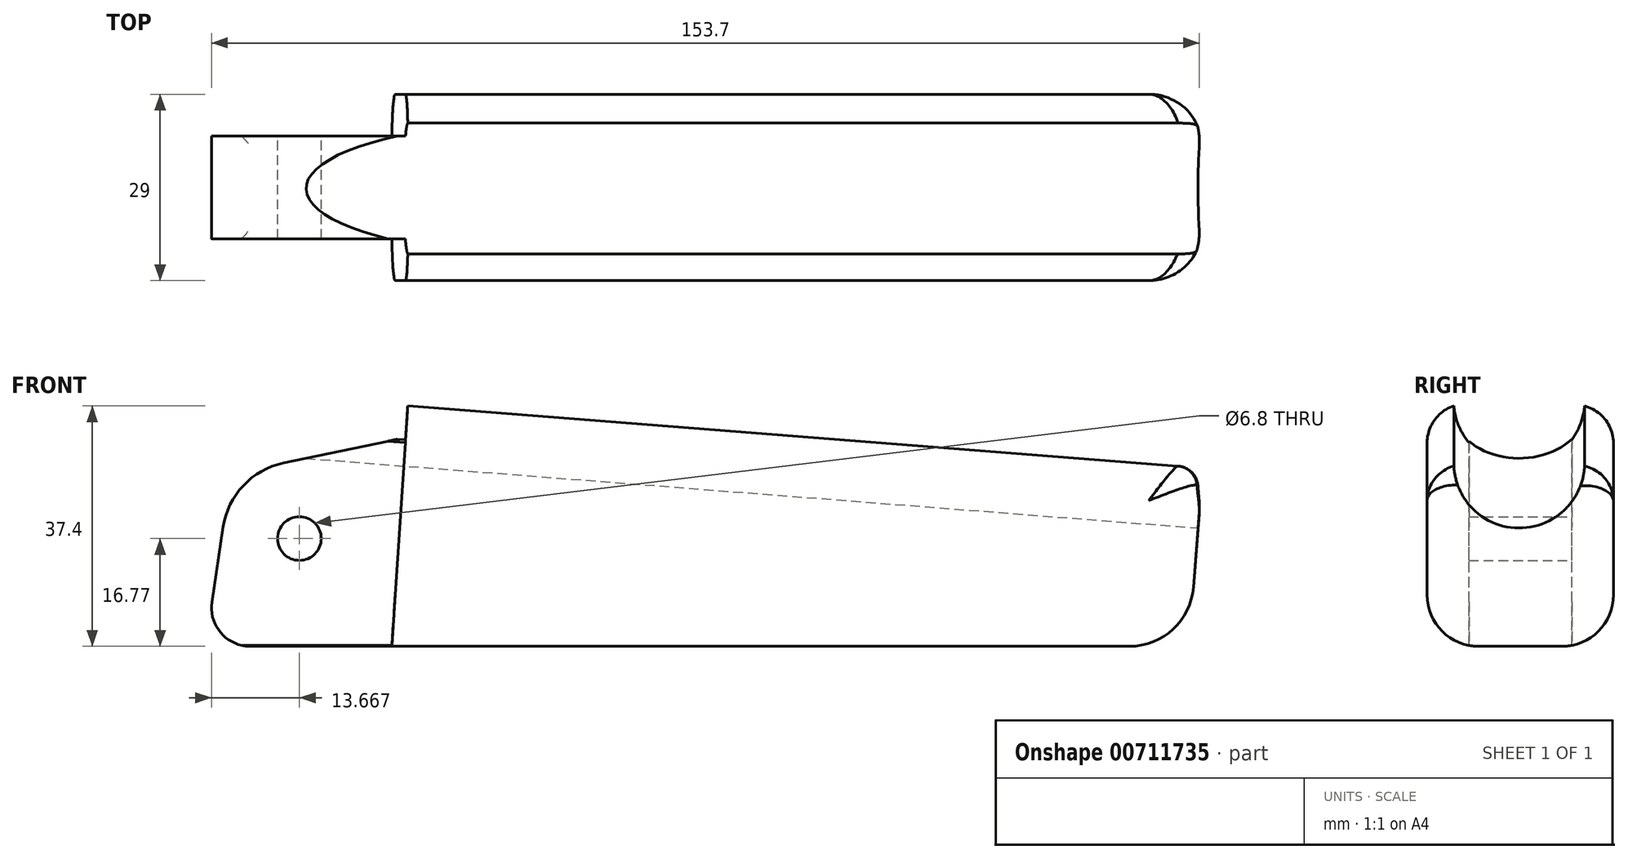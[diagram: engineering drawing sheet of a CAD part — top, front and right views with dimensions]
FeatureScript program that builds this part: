
annotation { "Feature Type Name" : "Feature", "Feature Type Description" : "" }
export const myFeature = defineFeature(function(context is Context, id is Id, definition is map)
    precondition{}
    {
        {
            var Q0;
            Q0=qCreatedBy(makeId("Front.planeOp"),FACE);
            var sketch = newSketch(context, id + "F0", { "sketchPlane" : qUnion([Q0])});
            skLineSegment(sketch, "E0", {"start": v(-23.94, 0) * mm, "end": v(100.06, 0) * mm});
            skLineSegment(sketch, "E1", {"start": v(-21.46, 37.4) * mm, "end": v(102.22, 27.74) * mm});
            skLineSegment(sketch, "E2", {"start": v(102.22, 27.74) * mm, "end": v(100.06, 0) * mm});
            skLineSegment(sketch, "E3", {"start": v(-23.94, 0) * mm, "end": v(-45.99, 0) * mm});
            skCircle(sketch, "E4", {"center": v(-38.32, 16.77) * mm, "radius": 3.4 * mm});
            skArc(sketch, "E5", {"start": v(-40.79, 28.51) * mm, "mid": v(-47.06, 25) * mm, "end": v(-50.2, 18.53) * mm});
            skLineSegment(sketch, "E6", {"start": v(-21.79, 32.5) * mm, "end": v(-40.79, 28.51) * mm});
            skLineSegment(sketch, "E7", {"start": v(-23.94, 0) * mm, "end": v(-21.46, 37.4) * mm});
            skLineSegment(sketch, "E8", {"start": v(-51.92, 6.88) * mm, "end": v(-50.2, 18.53) * mm});
            skArc(sketch, "E9.filletArc", {"start": v(-51.92, 6.88) * mm, "mid": v(-50.53, 2.08) * mm, "end": v(-45.99, 0) * mm});
            skSolve(sketch);
        }
        {
            var Q0;
            Q0=makeQuery(id+"F0.imprint","IMPRINT",FACE,{"disambiguationData":[TD([[makeQuery(id+"F0.imprint","IMPRINT",EDGE,{"derivedFrom":sQuery(id+"F0.wireOp",EDGE,"E0")}),1.0]])]});
            extrude(context, id + "F1", {"entities" : qUnion([Q0]), "endBound" : BoundingType.SYMMETRIC, "depth" : 29 * mm, "offsetDistance" : 25 * mm});
        }
        {
            var Q0;
            Q0 = qSketchRegion(id + "F0", true);
            extrude(context, id + "F2", {"entities" : qUnion([Q0]), "operationType" : NewBodyOperationType.ADD, "endBound" : BoundingType.SYMMETRIC, "depth" : 16 * mm, "offsetDistance" : 25 * mm});
        }
        {
            var Q0;
            Q0=makeQuery(id+"F1.opExtrude","SWEPT_FACE",FACE,{"disambiguationData":[OSD([sQuery(id+"F0.wireOp",EDGE,"E2")])]});
            var sketch = newSketch(context, id + "F3", { "sketchPlane" : qUnion([Q0])});
            skLineSegment(sketch, "E10", {"start": v(-27.87, 26.47) * mm, "end": v(29.15, 26.47) * mm, "construction": true});
            skLineSegment(sketch, "E11", {"start": v(10, 48.39) * mm, "end": v(10, -4.27) * mm, "construction": true});
            skLineSegment(sketch, "E12", {"start": v(-10, 48.02) * mm, "end": v(-10, 0) * mm, "construction": true});
            skCircle(sketch, "E13", {"center": v(-0.17, 36.45) * mm, "radius": 10.2 * mm});
            skPoint(sketch, "E13.first.point", {"position": v(-10, 33.7) * mm});
            skPoint(sketch, "E13.second.point", {"position": v(10, 35.62) * mm});
            skPoint(sketch, "E13.third.point", {"position": v(1.93, 26.47) * mm});
            skSolve(sketch);
        }
        {
            var Q0;
            {var subQ0=sQuery(id+"F3.wireOp",EDGE,"E13");var subQ1=makeQuery(id+"F1.opExtrude","SWEPT_EDGE",EDGE,{"disambiguationData":[OSD([sQuery(id+"F0.wireOp",EDGE,"E1"),sQuery(id+"F0.wireOp",EDGE,"E2")])]});var subQ2=makeQuery(id+"F3.imprint","INTERSECT",VERTEX,{"disambiguationData":[OD(0.0)],"derivedFrom":[subQ1,subQ0]});Q0=makeQuery(id+"F3.imprint","IMPRINT",FACE,{"disambiguationData":[TD([[makeQuery(id+"F3.imprint","IMPRINT",EDGE,{"disambiguationData":[TD([[subQ2,1.0]])],"derivedFrom":subQ0}),1.0]])]});}
            extrude(context, id + "F4", {"entities" : qUnion([Q0]), "operationType" : NewBodyOperationType.REMOVE, "endBound" : BoundingType.THROUGH_ALL, "oppositeDirection" : true, "depth" : 25 * mm, "offsetDistance" : 25 * mm});
        }
        {
            var Q0;
            Q0=makeQuery(id+"F1.opExtrude","CAP_EDGE",EDGE,{"disambiguationData":[OSD([sQuery(id+"F0.wireOp",EDGE,"E1")])],"isStart":false});
            var Q1;
            Q1=makeQuery(id+"F1.opExtrude","CAP_EDGE",EDGE,{"disambiguationData":[OSD([sQuery(id+"F0.wireOp",EDGE,"E1")])],"isStart":true});
            fillet(context, id + "F5", {"entities" : qUnion([Q0, Q1]), "radius" : 6 * mm, "tangentPropagation" : true, "allowEdgeOverflow" : false});
        }
        {
            var Q0;
            Q0=makeQuery(id+"F1.opExtrude","CAP_EDGE",EDGE,{"disambiguationData":[OSD([sQuery(id+"F0.wireOp",EDGE,"E0")])],"isStart":true});
            var Q1;
            Q1=makeQuery(id+"F1.opExtrude","CAP_EDGE",EDGE,{"disambiguationData":[OSD([sQuery(id+"F0.wireOp",EDGE,"E0")])],"isStart":false});
            var Q2;
            Q2=makeQuery(id+"F1.opExtrude","CAP_EDGE",EDGE,{"disambiguationData":[OSD([sQuery(id+"F0.wireOp",EDGE,"E2")])],"isStart":false});
            var Q3;
            Q3=makeQuery(id+"F1.opExtrude","CAP_EDGE",EDGE,{"disambiguationData":[OSD([sQuery(id+"F0.wireOp",EDGE,"E2")])],"isStart":true});
            fillet(context, id + "F6", {"entities" : qUnion([Q0, Q1, Q2, Q3]), "radius" : 8 * mm, "tangentPropagation" : true, "allowEdgeOverflow" : false});
        }
        {
            var Q0;
            {var subQ0=sQuery(id+"F0.wireOp",EDGE,"E1");Q0=makeQuery(id+"F6.opFillet","BLEND_EDGE",EDGE,{"blendedFrom":[makeQuery(id+"F1.opExtrude","CAP_EDGE",EDGE,{"disambiguationData":[OSD([sQuery(id+"F0.wireOp",EDGE,"E2")])],"isStart":false}),makeQuery(id+"F5.opFillet","BLEND_FACE",FACE,{"disambiguationData":[OSD([subQ0]),TDD([makeQuery(id+"F1.opExtrude","CAP_EDGE",EDGE,{"disambiguationData":[OSD([subQ0])],"isStart":false})])]})],"blendedInto":[makeQuery(id+"F5.opFillet","BLEND_FACE",FACE,{"disambiguationData":[OSD([subQ0]),TDD([makeQuery(id+"F1.opExtrude","CAP_EDGE",EDGE,{"disambiguationData":[OSD([subQ0])],"isStart":false})])]})]});}
            var Q1;
            {var subQ0=sQuery(id+"F0.wireOp",EDGE,"E1");Q1=makeQuery(id+"F6.opFillet","BLEND_EDGE",EDGE,{"blendedFrom":[makeQuery(id+"F1.opExtrude","CAP_EDGE",EDGE,{"disambiguationData":[OSD([sQuery(id+"F0.wireOp",EDGE,"E2")])],"isStart":true}),makeQuery(id+"F5.opFillet","BLEND_FACE",FACE,{"disambiguationData":[OSD([subQ0]),TDD([makeQuery(id+"F1.opExtrude","CAP_EDGE",EDGE,{"disambiguationData":[OSD([subQ0])],"isStart":true})])]})],"blendedInto":[makeQuery(id+"F5.opFillet","BLEND_FACE",FACE,{"disambiguationData":[OSD([subQ0]),TDD([makeQuery(id+"F1.opExtrude","CAP_EDGE",EDGE,{"disambiguationData":[OSD([subQ0])],"isStart":true})])]})]});}
            fillet(context, id + "F7", {"entities" : qUnion([Q0, Q1]), "radius" : 3 * mm, "tangentPropagation" : true, "allowEdgeOverflow" : false});
        }
        {
            var Q0;
            Q0=makeQuery(id+"F1.opExtrude","SWEPT_EDGE",EDGE,{"disambiguationData":[OSD([sQuery(id+"F0.wireOp",EDGE,"E0"),sQuery(id+"F0.wireOp",EDGE,"E2")])]});
            fillet(context, id + "F8", {"entities" : qUnion([Q0]), "radius" : 10 * mm, "tangentPropagation" : true, "allowEdgeOverflow" : false});
        }
    });
